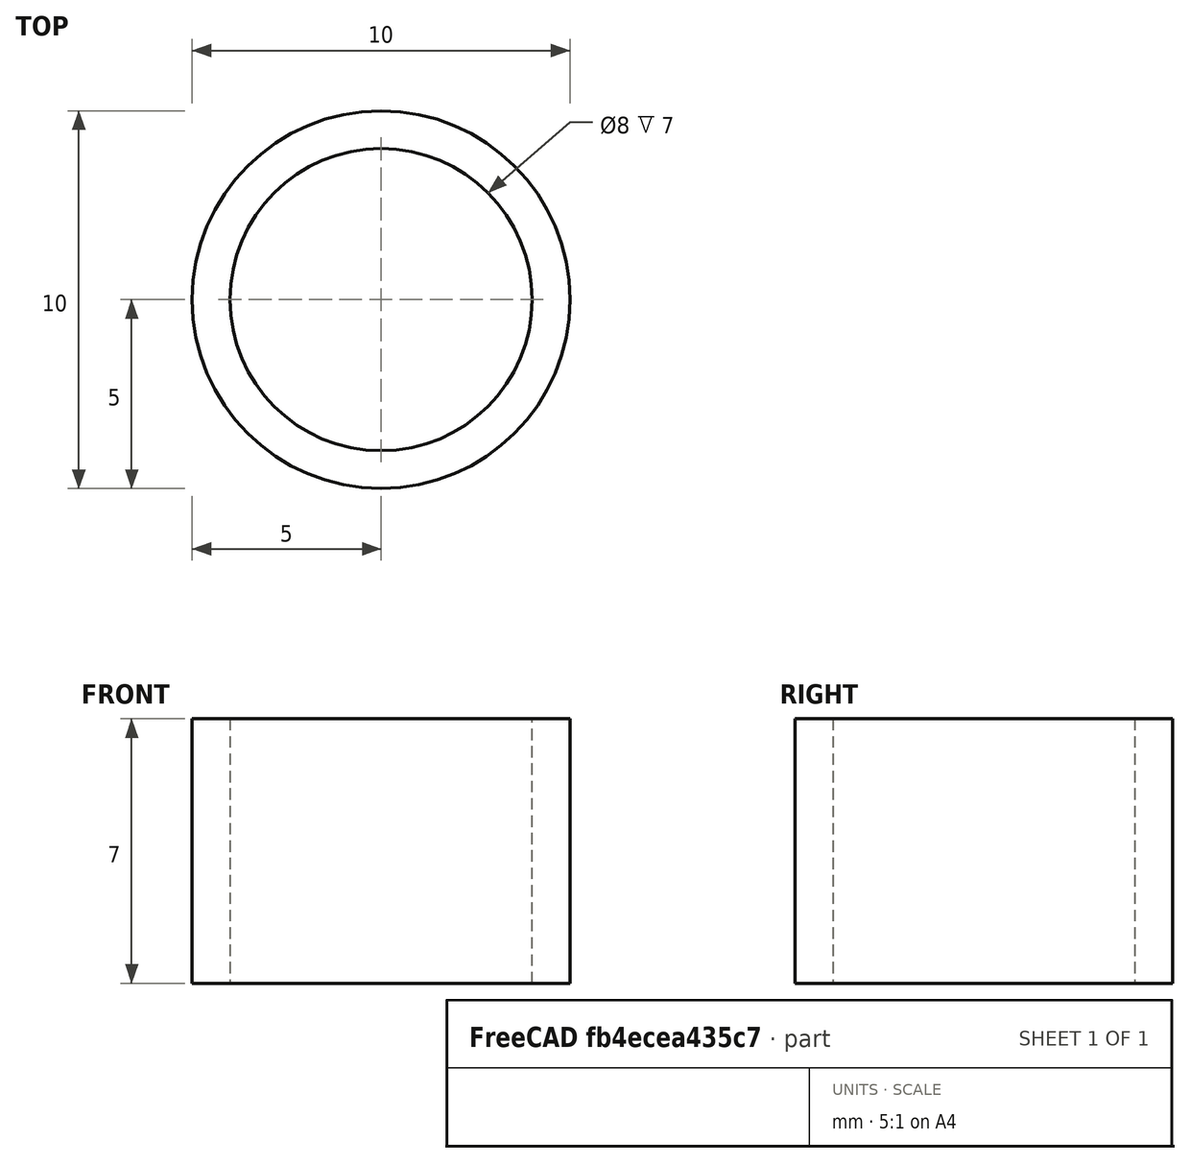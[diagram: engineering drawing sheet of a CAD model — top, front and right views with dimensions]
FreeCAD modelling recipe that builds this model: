
FCSTD DOCUMENT  (FreeCAD 0.19R24276 (Git))
Label: Ring_10x8
License: All rights reserved
LicenseURL: http://en.wikipedia.org/wiki/All_rights_reserved
objects: Sketcher::SketchObject×1, PartDesign::Pad×1, PartDesign::Body×1
note: 4 computed .brp shape members not serialized (recipe doc carries the construction recipe); baked Part::Feature solids carry a one-line shape summary decoded from their .brp

FEATURE [Sketcher::SketchObject] Sketch
  FullyConstrained = true
  MapMode = 5
  Support = -> [XY_Plane]
  sketch-geometry (2):
    g0: Circle CenterX=0 CenterY=0 CenterZ=0 NormalX=0 NormalY=0 NormalZ=1 AngleXU=0 Radius=5
    g1: Circle CenterX=0 CenterY=0 CenterZ=0 NormalX=0 NormalY=0 NormalZ=1 AngleXU=0 Radius=4
  constraints (4):
    c: Coincident(g1,g0)
    c: Diameter(g1) = 8
    c: Diameter(g0) = 10
    c: Coincident(g0,g-1)
FEATURE [PartDesign::Pad] Pad
  Direction = (1,1,1)
  Length = 7
  Length2 = 100
  Profile = -> Sketch
  Type = 0
FEATURE [PartDesign::Body] Body
  Group = -> [Sketch,Pad]
  Origin = -> Origin
  Tip = -> Pad
